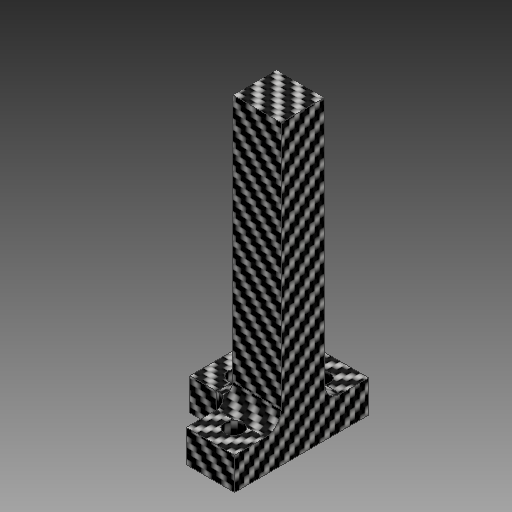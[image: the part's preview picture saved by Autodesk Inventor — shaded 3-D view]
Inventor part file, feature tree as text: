
AUTODESK INVENTOR PART (.ipt)
format: ipt  version: 2018 (Build 220112000, 112)  size: 243,712 bytes
history: native  units: mm
features: sketch x5, other x3
ambient origin geometry x8: Origin, YZ Plane, XZ Plane, XY Plane, X Axis, Y Axis, Z Axis, Center Point
bodies: Volumenkörper1 (feature_tree)
feature tree (8):
  other  "SolarpanelHalterung1_MIR2.ipt"
  other  "Volumenkörper1::SolarpanelHalterung1_MIR2.ipt"
  other  "Bezeichnung1"
  sketch  "Skizze1"  dims[d0=10.0mm]
  sketch  "Skizze2"
  sketch  "Skizze3"
  sketch  "Skizze4"
  sketch  "Skizze5"
